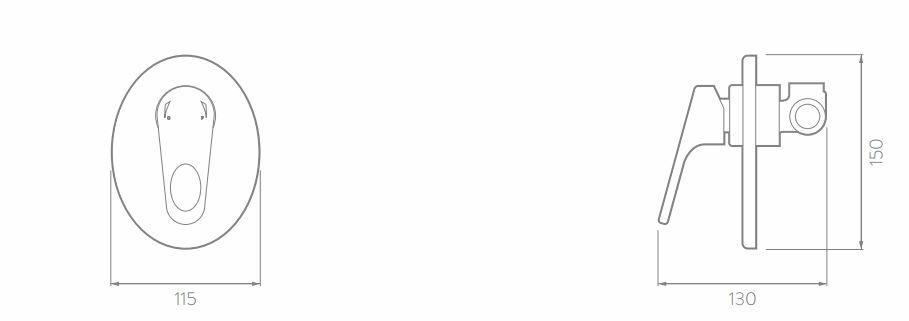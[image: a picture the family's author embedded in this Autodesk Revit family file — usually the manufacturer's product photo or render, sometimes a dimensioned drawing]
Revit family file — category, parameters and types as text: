
# Revit family: KR4035551_Ducha Monocontrol Koral PRO SSB
name_source: partatom
category: Plumbing Fixtures
units: mm (PartAtom-declared; Revit-internal decimal feet)

## family parameters
Always vertical = Yes
Cut with Voids When Loaded = No
Host = Wall
OmniClass Number = 23.45.05.14.17
OmniClass Title = Showers
Part Type = Normal
Room Calculation Point = No
Round Connector Dimension = Use Diameter
Shared = No

## types (1)
- Type 1
    Alto = 946 mm
    Altura ducha = 2000 mm  [stored 6.56168 ft]
    Altura mezclador = 1200 mm
    Ancho = 152 mm
    Capacidad de flujo = 80 psi: 9,3 L/min
    Fabricante = Corona
    Garantía = 30 años
    Material = Corona_Acero
    Peso neto = 1.200 g. - 2,60 lb
    Presion maxima = 125 psi (860 kPa)
    Presion minima = 20 psi (140 kPa)
    Profundidad = 329 mm  [stored 1.0794 ft]
    Referencia = KR4075551
    Temperatura de uso = 5˚C a 71˚C
    URL = https://corona.co

note: [stored X ft] marks values corroborated as IEEE doubles in the binary element streams (Revit-internal decimal feet)

## geometry (parser evidence)
native form markers: Sweep x10
no freeform markers — native parametric forms only
